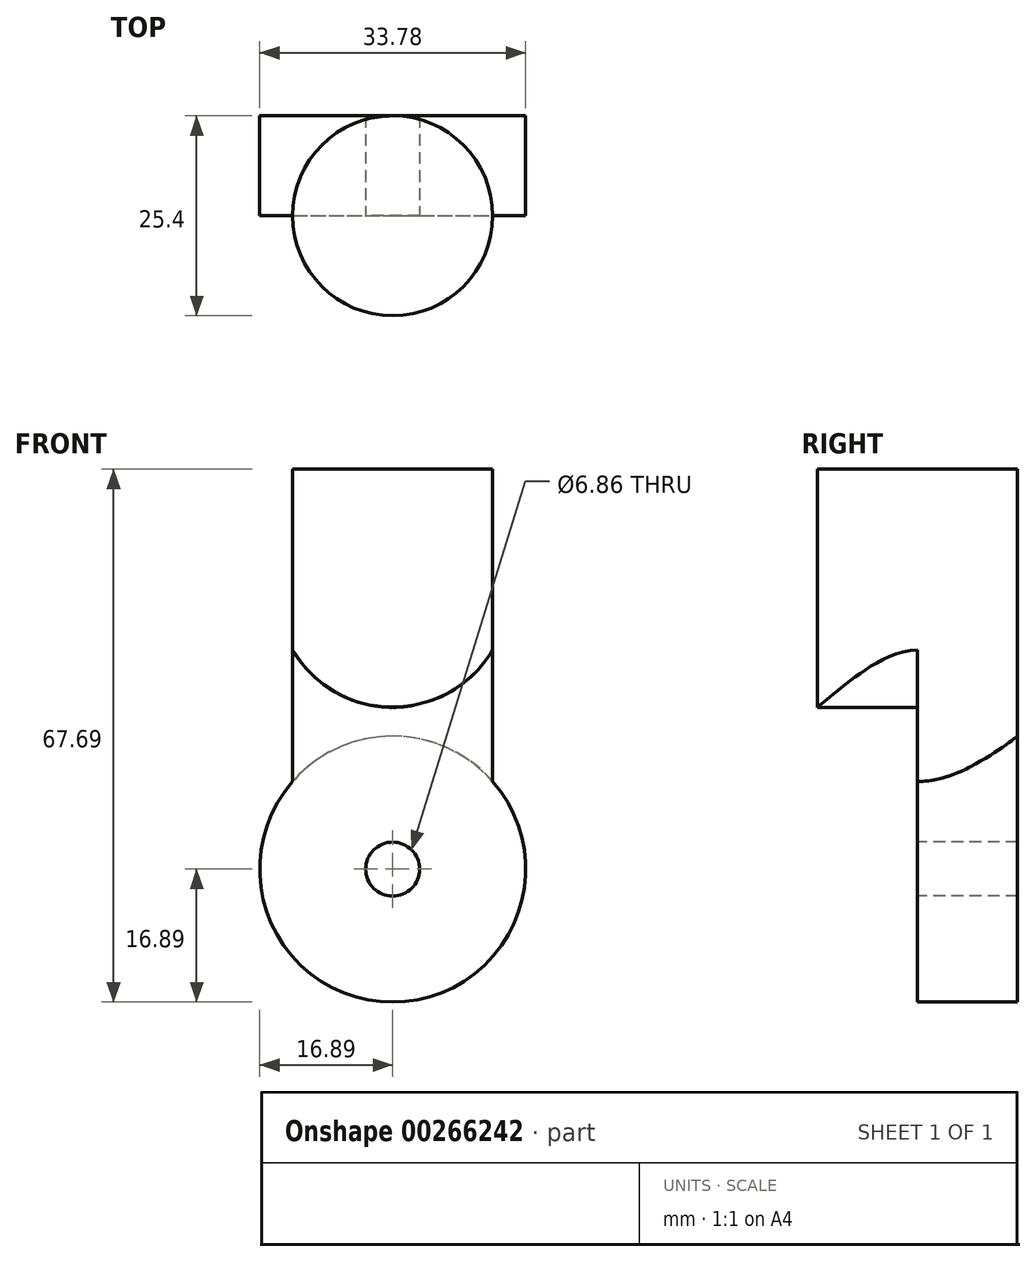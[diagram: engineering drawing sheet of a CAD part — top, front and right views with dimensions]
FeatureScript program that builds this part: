
annotation { "Feature Type Name" : "Feature", "Feature Type Description" : "" }
export const myFeature = defineFeature(function(context is Context, id is Id, definition is map)
    precondition{}
    {
        {
            var Q0;
            Q0=qCreatedBy(makeId("Front.planeOp"),FACE);
            var sketch = newSketch(context, id + "F0", { "sketchPlane" : qUnion([Q0])});
            skCircle(sketch, "E0", {"center": v(0, 0) * mm, "radius": 16.9 * mm});
            skSolve(sketch);
        }
        {
            var Q0;
            Q0=qSketchRegion(id+"F0",true);
            extrude(context, id + "F1", {"entities" : qUnion([Q0]), "endBound" : BoundingType.SYMMETRIC, "depth" : 25.4 * mm});
        }
        {
            var Q0;
            Q0=qCreatedBy(makeId("Top.planeOp"),FACE);
            var sketch = newSketch(context, id + "F2", { "sketchPlane" : qUnion([Q0])});
            skCircle(sketch, "E1", {"center": v(0, 0) * mm, "radius": 12.7 * mm});
            skLineSegment(sketch, "E2", {"start": v(20.17, 0) * mm, "end": v(-31.4, 0) * mm, "construction": true});
            skSolve(sketch);
        }
        {
            var Q0;
            Q0=qSketchRegion(id+"F2",true);
            extrude(context, id + "F3", {"entities" : qUnion([Q0]), "operationType" : NewBodyOperationType.ADD, "depth" : 50.8 * mm});
        }
        {
            var Q0;
            Q0=qCreatedBy(makeId("Front.planeOp"),FACE);
            cPlane(context, id + "F4", {"entities" : qUnion([Q0]), "cplaneType" : CPlaneType.OFFSET, "offset" : 12.7 * mm, "width" : 152.4 * mm, "height" : 152.4 * mm});
        }
        {
            var Q0;
            Q0=qCreatedBy(id+"F4.planeOp",FACE);
            var sketch = newSketch(context, id + "F5", { "sketchPlane" : qUnion([Q0])});
            skCircle(sketch, "E3", {"center": v(0, 0) * mm, "radius": 16.9 * mm});
            skSolve(sketch);
        }
        {
            var Q0;
            Q0=qSketchRegion(id+"F5",true);
            var Q1;
            Q1=makeQuery(id+"F1.opExtrude","CAP_FACE",FACE,{"disambiguationData":[OSD([sQuery(id+"F0.wireOp",EDGE,"E0")])],"isStart":false});
            extrude(context, id + "F6", {"entities" : qUnion([Q0]), "operationType" : NewBodyOperationType.REMOVE, "oppositeDirection" : true, "endBoundEntityFace" : qUnion([Q1]), "depth" : 12.7 * mm});
        }
        {
            var Q0;
            Q0=makeQuery(id+"F6.boolean.opBoolean","COPY",FACE,{"derivedFrom":makeQuery(id+"F6.opExtrude","CAP_FACE",FACE,{"disambiguationData":[OSD([sQuery(id+"F5.wireOp",EDGE,"E3")])],"isStart":false})});
            var sketch = newSketch(context, id + "F7", { "sketchPlane" : qUnion([Q0])});
            skCircle(sketch, "E4", {"center": v(0, 0) * mm, "radius": 3.43 * mm});
            skSolve(sketch);
        }
        {
            var Q0;
            Q0=qSketchRegion(id+"F7",true);
            extrude(context, id + "F8", {"entities" : qUnion([Q0]), "operationType" : NewBodyOperationType.REMOVE, "endBound" : BoundingType.THROUGH_ALL, "oppositeDirection" : true, "depth" : 25.4 * mm});
        }
        {
            var Q0;
            Q0=qCreatedBy(id+"F4.planeOp",FACE);
            var sketch = newSketch(context, id + "F9", { "sketchPlane" : qUnion([Q0])});
            skArc(sketch, "E5", {"start": v(-13.43, 29.26) * mm, "mid": v(0, 20.56) * mm, "end": v(13.43, 29.26) * mm});
            skLineSegment(sketch, "E6.bottom", {"start": v(13.43, 29.26) * mm, "end": v(13.45, 29.26) * mm});
            skLineSegment(sketch, "E6.top", {"start": v(-13.43, 6.1) * mm, "end": v(13.45, 6.1) * mm});
            skLineSegment(sketch, "E6.left", {"start": v(-13.43, 29.26) * mm, "end": v(-13.43, 6.1) * mm});
            skLineSegment(sketch, "E6.right", {"start": v(13.45, 29.26) * mm, "end": v(13.45, 6.1) * mm});
            skPoint(sketch, "E7.orphan", {"position": v(-14.72, 35.29) * mm});
            skSolve(sketch);
        }
        {
            var Q0;
            Q0=qSketchRegion(id+"F9",true);
            var Q1;
            Q1=makeQuery(id+"F6.boolean.opBoolean","COPY",FACE,{"derivedFrom":makeQuery(id+"F6.opExtrude","CAP_FACE",FACE,{"disambiguationData":[OSD([sQuery(id+"F5.wireOp",EDGE,"E3")])],"isStart":false})});
            extrude(context, id + "F10", {"entities" : qUnion([Q0]), "operationType" : NewBodyOperationType.REMOVE, "endBound" : BoundingType.UP_TO_SURFACE, "oppositeDirection" : true, "endBoundEntityFace" : qUnion([Q1]), "depth" : 25.4 * mm});
        }
    });
